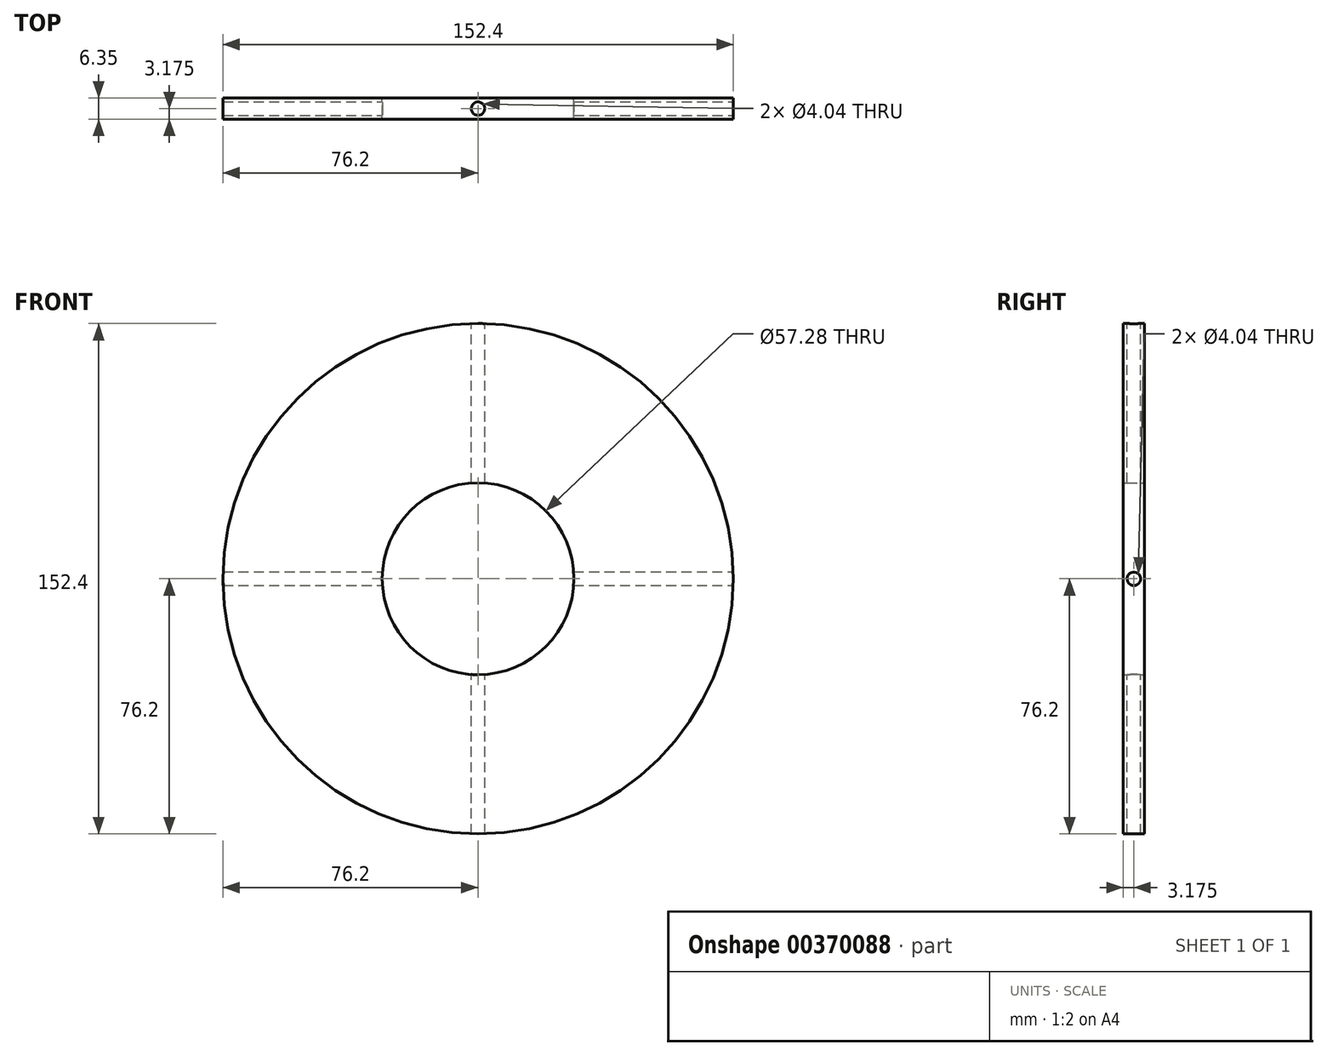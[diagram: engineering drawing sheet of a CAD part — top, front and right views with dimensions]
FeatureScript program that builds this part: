
annotation { "Feature Type Name" : "Feature", "Feature Type Description" : "" }
export const myFeature = defineFeature(function(context is Context, id is Id, definition is map)
    precondition{}
    {
        {
            var Q0;
            Q0=qCreatedBy(makeId("Front.planeOp"),FACE);
            var sketch = newSketch(context, id + "F0", { "sketchPlane" : qUnion([Q0])});
            skCircle(sketch, "E0", {"center": v(0, 0) * mm, "radius": 28.64 * mm});
            skCircle(sketch, "E1", {"center": v(0, 0) * mm, "radius": 76.2 * mm});
            skSolve(sketch);
        }
        {
            var Q0;
            Q0=makeQuery(id+"F0.imprint","IMPRINT",FACE,{"disambiguationData":[TD([[makeQuery(id+"F0.imprint","IMPRINT",EDGE,{"derivedFrom":sQuery(id+"F0.wireOp",EDGE,"E0")}),-1.0]])]});
            extrude(context, id + "F1", {"entities" : qUnion([Q0]), "depth" : 6.35 * mm});
        }
        {
            var Q0;
            Q0=qCreatedBy(makeId("Top.planeOp"),FACE);
            cPlane(context, id + "F2", {"entities" : qUnion([Q0]), "cplaneType" : CPlaneType.OFFSET, "offset" : 76.2 * mm, "width" : 152.4 * mm, "height" : 152.4 * mm});
        }
        {
            var Q0;
            Q0=qCreatedBy(id+"F2.planeOp",FACE);
            var sketch = newSketch(context, id + "F3", { "sketchPlane" : qUnion([Q0])});
            skLineSegment(sketch, "E2", {"start": v(0, 0) * mm, "end": v(0, -3.18) * mm});
            skSolve(sketch);
        }
        {
            var Q0;
            Q0=sQuery(id+"F3.wireOp",VERTEX,"ivMhsvMC-Tzgr-ZYih-3o8P-cT3DylMsyFpw.center");
            var Q1;
            Q1=sQuery(id+"F3.wireOp",VERTEX,"E2.end");
            var Q2;
            Q2=makeQuery(id+"F1.opExtrude","SWEPT_BODY",BODY,{"disambiguationData":[OSD([sQuery(id+"F0.wireOp",EDGE,"E0"),sQuery(id+"F0.wireOp",EDGE,"E1")])]});
            hole(context, id + "F4", {"style" : HoleStyle.SIMPLE, "endStyle" : HoleEndStyle.THROUGH, "standardTappedOrClearance" : lookupTablePath({ "standard" : "ANSI", "engagement" : "75%", "pitch" : "32 tpi", "size" : "#10", "type" : "Tapped" }), "standardBlindInLast" : lookupTablePath({ "standard" : "ANSI", "engagement" : "75%", "pitch" : "32 tpi", "size" : "#10", "type" : "Tapped" }), "holeDiameter" : 4.04 * mm, "showTappedDepth" : true, "isTappedThrough" : true, "tappedDepth" : 12.7 * mm, "tapClearance" : 3, "locations" : qUnion([Q0, Q1]), "scope" : qUnion([Q2]), "majorDiameter" : 4.83 * mm});
        }
        {
            var Q0;
            Q0=qCreatedBy(makeId("Right.planeOp"),FACE);
            cPlane(context, id + "F5", {"entities" : qUnion([Q0]), "cplaneType" : CPlaneType.OFFSET, "offset" : 76.2 * mm, "width" : 152.4 * mm, "height" : 152.4 * mm});
        }
        {
            var Q0;
            Q0=qCreatedBy(id+"F5.planeOp",FACE);
            var sketch = newSketch(context, id + "F6", { "sketchPlane" : qUnion([Q0])});
            skLineSegment(sketch, "E3", {"start": v(0, 0) * mm, "end": v(-3.18, 0) * mm});
            skSolve(sketch);
        }
        {
            var Q0;
            Q0=sQuery(id+"F6.wireOp",VERTEX,"E3.end");
            var Q1;
            Q1=makeQuery(id+"F1.opExtrude","SWEPT_BODY",BODY,{"disambiguationData":[OSD([sQuery(id+"F0.wireOp",EDGE,"E0"),sQuery(id+"F0.wireOp",EDGE,"E1")])]});
            hole(context, id + "F7", {"style" : HoleStyle.SIMPLE, "endStyle" : HoleEndStyle.THROUGH, "standardTappedOrClearance" : lookupTablePath({ "standard" : "ANSI", "engagement" : "75%", "pitch" : "32 tpi", "size" : "#10", "type" : "Tapped" }), "standardBlindInLast" : lookupTablePath({ "standard" : "ANSI", "engagement" : "75%", "pitch" : "32 tpi", "size" : "#10", "type" : "Tapped" }), "holeDiameter" : 4.04 * mm, "showTappedDepth" : true, "isTappedThrough" : true, "tappedDepth" : 12.7 * mm, "tapClearance" : 3, "locations" : qUnion([Q0]), "scope" : qUnion([Q1]), "majorDiameter" : 4.83 * mm});
        }
    });
